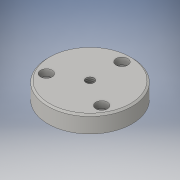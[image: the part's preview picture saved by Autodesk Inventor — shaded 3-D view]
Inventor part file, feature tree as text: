
AUTODESK INVENTOR PART (.ipt)
format: ipt  version: 2016 (Build 200138000, 138)  size: 120,320 bytes
history: native  units: mm
features: sketch x3, hole x2, extrude x1, chamfer x1
ambient origin geometry x8: Origin, YZ Plane, XZ Plane, XY Plane, X Axis, Y Axis, Z Axis, Center Point
bodies: Solid1 (feature_tree)
feature tree (7):
  extrude  "Extrusion1"  Depth=10.0mm TaperAngle=0.0deg
  hole  "Hole1"  [1 undecoded]
  hole  "Hole2"  [1 undecoded]
  chamfer  "Chamfer1"  Distance=2.0mm Angle=45.0deg
  sketch  "Sketch1"  dims[d0=50.0mm d1=10.0mm d2=0.0mm]
  sketch  "Sketch2"  dims[d3=4.917mm d4=12.0mm d5=4.0mm d6=2.0mm d7=90.0deg d8=17.1mm d9=20.594885mm d10=38.0mm]
  sketch  "Sketch3"  dims[d11=120.0deg d12=120.0deg d13=4.0mm d14=4.0mm d15=7.0mm d16=4.0mm d17=90.0deg d18=17.1mm d19=20.594885mm d20=1.0mm d21=2.0mm d22=45.0deg]
note: 2 required parameter values undecoded (feature->parameter linkage not recoverable at this tier; creation-order binding heuristic only, values carry confidence <= 0.55)
